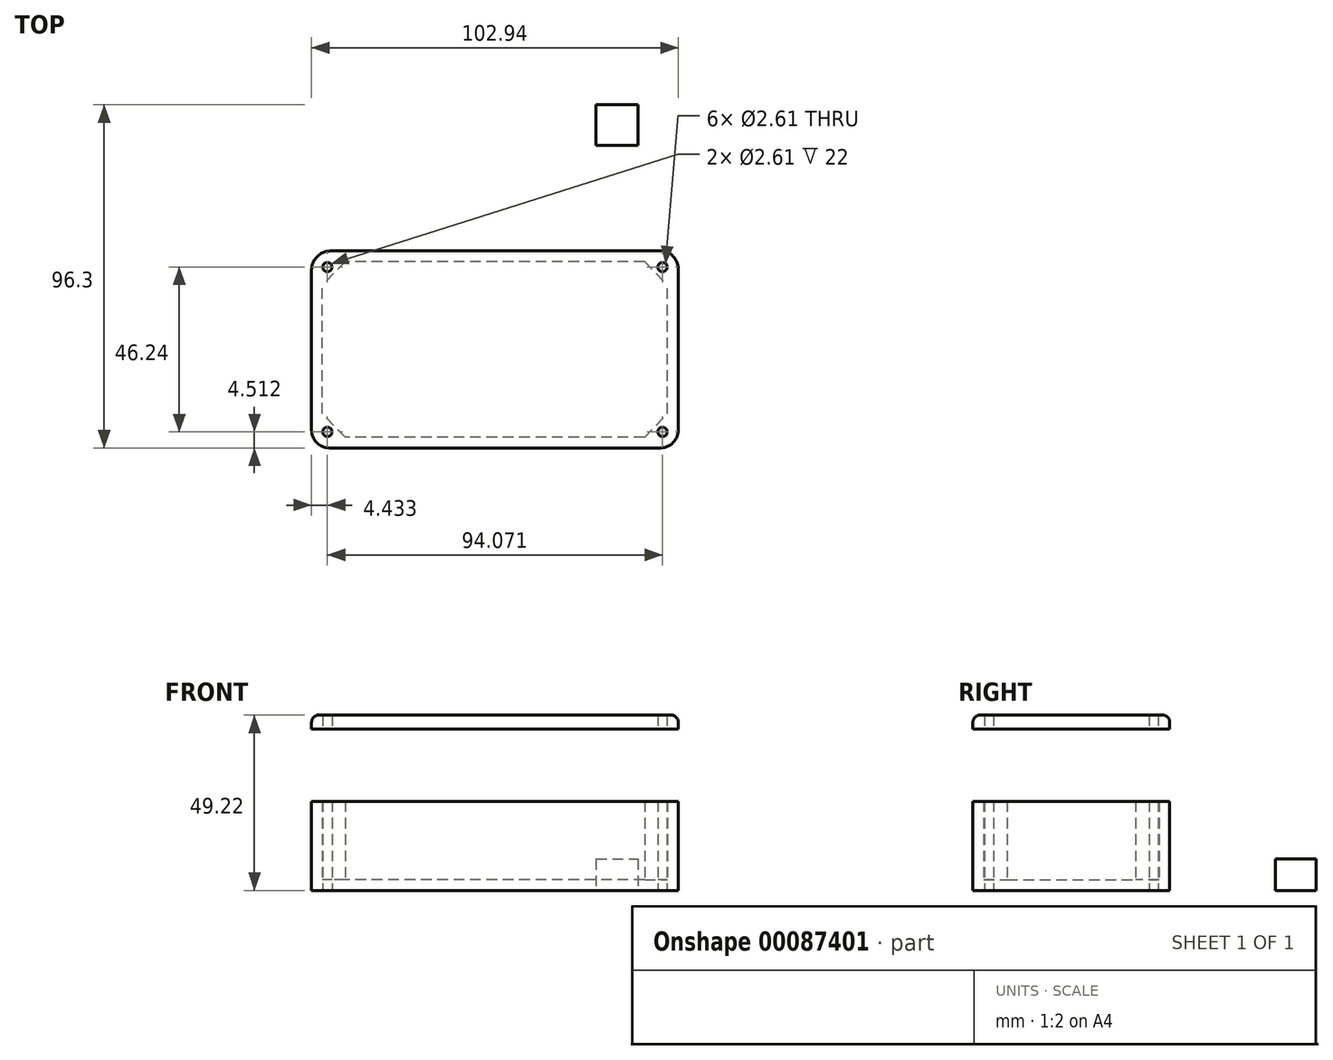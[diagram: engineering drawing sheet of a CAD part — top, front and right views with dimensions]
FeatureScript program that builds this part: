
annotation { "Feature Type Name" : "Feature", "Feature Type Description" : "" }
export const myFeature = defineFeature(function(context is Context, id is Id, definition is map)
    precondition{}
    {
        {
            var Q0;
            Q0=qCreatedBy(makeId("Top.planeOp"),FACE);
            var sketch = newSketch(context, id + "F0", { "sketchPlane" : qUnion([Q0])});
            skLineSegment(sketch, "E0.bottom", {"start": v(-57.78, 29.78) * mm, "end": v(34.86, 29.78) * mm});
            skLineSegment(sketch, "E0.top", {"start": v(-58.08, -25.48) * mm, "end": v(34.86, -25.48) * mm});
            skLineSegment(sketch, "E0.left", {"start": v(-63.08, 24.48) * mm, "end": v(-63.08, -20.48) * mm});
            skLineSegment(sketch, "E0.right", {"start": v(39.86, 24.78) * mm, "end": v(39.86, -20.48) * mm});
            skLineSegment(sketch, "E1.bottom", {"start": v(-11.61, 29.78) * mm, "end": v(-11.61, 29.78) * mm});
            skLineSegment(sketch, "E1.top", {"start": v(-11.61, -25.48) * mm, "end": v(-11.61, -25.48) * mm});
            skLineSegment(sketch, "E1.left", {"start": v(-11.61, 29.78) * mm, "end": v(-11.61, -25.48) * mm, "construction": true});
            skLineSegment(sketch, "E1.right", {"start": v(-11.61, 29.78) * mm, "end": v(-11.61, -25.48) * mm, "construction": true});
            skLineSegment(sketch, "E2", {"start": v(-63.08, 2.15) * mm, "end": v(39.86, 2.15) * mm, "construction": true});
            skPoint(sketch, "E3.visualSharp", {"position": v(-63.08, 29.78) * mm});
            skArc(sketch, "E3.filletArc", {"start": v(-57.78, 29.78) * mm, "mid": v(-61.53, 28.23) * mm, "end": v(-63.08, 24.48) * mm});
            skPoint(sketch, "E4.visualSharp", {"position": v(39.86, 29.78) * mm});
            skArc(sketch, "E4.filletArc", {"start": v(39.86, 24.78) * mm, "mid": v(38.4, 28.32) * mm, "end": v(34.86, 29.78) * mm});
            skPoint(sketch, "E5.visualSharp", {"position": v(39.86, -25.48) * mm});
            skArc(sketch, "E5.filletArc", {"start": v(34.86, -25.48) * mm, "mid": v(38.4, -24.01) * mm, "end": v(39.86, -20.48) * mm});
            skPoint(sketch, "E6.visualSharp", {"position": v(-63.08, -25.48) * mm});
            skArc(sketch, "E6.filletArc", {"start": v(-63.08, -20.48) * mm, "mid": v(-61.62, -24.01) * mm, "end": v(-58.08, -25.48) * mm});
            skArc(sketch, "E7.0", {"start": v(-57.78, 26.78) * mm, "mid": v(-59.4, 26.1) * mm, "end": v(-60.08, 24.48) * mm});
            skLineSegment(sketch, "E7.1", {"start": v(-57.78, 26.78) * mm, "end": v(34.86, 26.78) * mm});
            skLineSegment(sketch, "E7.2", {"start": v(-60.08, 24.48) * mm, "end": v(-60.08, -20.48) * mm});
            skArc(sketch, "E7.3", {"start": v(36.86, 24.78) * mm, "mid": v(36.27, 26.2) * mm, "end": v(34.86, 26.78) * mm});
            skArc(sketch, "E7.4", {"start": v(-60.08, -20.48) * mm, "mid": v(-59.5, -21.9) * mm, "end": v(-58.08, -22.48) * mm});
            skLineSegment(sketch, "E7.5", {"start": v(-58.08, -22.48) * mm, "end": v(34.86, -22.48) * mm});
            skArc(sketch, "E7.6", {"start": v(34.86, -22.48) * mm, "mid": v(36.27, -21.9) * mm, "end": v(36.86, -20.48) * mm});
            skLineSegment(sketch, "E7.7", {"start": v(36.86, 24.78) * mm, "end": v(36.86, -20.48) * mm});
            skCircle(sketch, "E8", {"center": v(-58.65, 25.27) * mm, "radius": 1.3 * mm});
            skLineSegment(sketch, "E9", {"start": v(-60.08, 20.2) * mm, "end": v(-53.64, 26.78) * mm});
            skCircle(sketch, "E10.MirrorC", {"center": v(35.42, 25.27) * mm, "radius": 1.3 * mm});
            skLineSegment(sketch, "E11.MirrorCS", {"start": v(36.86, 20.2) * mm, "end": v(30.41, 26.78) * mm});
            skCircle(sketch, "E12.MirrorC", {"center": v(35.42, -20.97) * mm, "radius": 1.3 * mm});
            skCircle(sketch, "E13.MirrorC", {"center": v(-58.65, -20.97) * mm, "radius": 1.3 * mm});
            skLineSegment(sketch, "E14.MirrorCS", {"start": v(-60.08, -15.9) * mm, "end": v(-53.64, -22.48) * mm});
            skLineSegment(sketch, "E15.MirrorCS", {"start": v(36.86, -15.9) * mm, "end": v(30.41, -22.48) * mm});
            skSolve(sketch);
        }
        {
            var Q0;
            Q0=qCreatedBy(makeId("Top.planeOp"),FACE);
            var sketch = newSketch(context, id + "F1", { "sketchPlane" : qUnion([Q0])});
            skLineSegment(sketch, "E16.bottom", {"start": v(16.8, 59.44) * mm, "end": v(28.5, 59.44) * mm});
            skLineSegment(sketch, "E16.top", {"start": v(16.8, 70.82) * mm, "end": v(28.5, 70.82) * mm});
            skLineSegment(sketch, "E16.left", {"start": v(16.8, 59.44) * mm, "end": v(16.8, 70.82) * mm});
            skLineSegment(sketch, "E16.right", {"start": v(28.5, 59.44) * mm, "end": v(28.5, 70.82) * mm});
            skSolve(sketch);
        }
        {
            var Q0;
            Q0=makeQuery(id+"F1.imprint","IMPRINT",FACE,{"disambiguationData":[TD([[makeQuery(id+"F1.imprint","IMPRINT",EDGE,{"derivedFrom":sQuery(id+"F1.wireOp",EDGE,"E16.bottom")}),1.0]])]});
            extrude(context, id + "F2", {"entities" : qUnion([Q0]), "depth" : 8.8 * mm});
        }
        {
            var Q0;
            {var subQ5=sQuery(id+"F0.wireOp",EDGE,"E9");Q0=makeQuery(id+"F0.imprint","IMPRINT",FACE,{"disambiguationData":[TD([[makeQuery(id+"F0.imprint","IMPRINT",EDGE,{"derivedFrom":subQ5}),-1.0]])]});}
            var Q1;
            Q1=makeQuery(id+"F0.imprint","IMPRINT",FACE,{"disambiguationData":[TD([[makeQuery(id+"F0.imprint","IMPRINT",EDGE,{"derivedFrom":sQuery(id+"F0.wireOp",EDGE,"E8")}),1.0]])]});
            var Q2;
            Q2=makeQuery(id+"F0.imprint","IMPRINT",FACE,{"disambiguationData":[TD([[makeQuery(id+"F0.imprint","IMPRINT",EDGE,{"derivedFrom":sQuery(id+"F0.wireOp",EDGE,"E13.MirrorC")}),-1.0]])]});
            var Q3;
            {var subQ1=sQuery(id+"F0.wireOp",EDGE,"E7.3");Q3=makeQuery(id+"F0.imprint","IMPRINT",FACE,{"disambiguationData":[TD([[makeQuery(id+"F0.imprint","IMPRINT",EDGE,{"derivedFrom":subQ1}),1.0]])]});}
            var Q4;
            {var subQ1=sQuery(id+"F0.wireOp",EDGE,"E7.4");Q4=makeQuery(id+"F0.imprint","IMPRINT",FACE,{"disambiguationData":[TD([[makeQuery(id+"F0.imprint","IMPRINT",EDGE,{"derivedFrom":subQ1}),1.0]])]});}
            var Q5;
            {var subQ1=sQuery(id+"F0.wireOp",EDGE,"E7.6");Q5=makeQuery(id+"F0.imprint","IMPRINT",FACE,{"disambiguationData":[TD([[makeQuery(id+"F0.imprint","IMPRINT",EDGE,{"derivedFrom":subQ1}),1.0]])]});}
            var Q6;
            Q6=makeQuery(id+"F0.imprint","IMPRINT",FACE,{"disambiguationData":[TD([[makeQuery(id+"F0.imprint","IMPRINT",EDGE,{"derivedFrom":sQuery(id+"F0.wireOp",EDGE,"E0.bottom")}),-1.0]])]});
            var Q7;
            Q7=makeQuery(id+"F0.imprint","IMPRINT",FACE,{"disambiguationData":[TD([[makeQuery(id+"F0.imprint","IMPRINT",EDGE,{"derivedFrom":sQuery(id+"F0.wireOp",EDGE,"E10.MirrorC")}),-1.0]])]});
            var Q8;
            {var subQ1=sQuery(id+"F0.wireOp",EDGE,"E7.0");Q8=makeQuery(id+"F0.imprint","IMPRINT",FACE,{"disambiguationData":[TD([[makeQuery(id+"F0.imprint","IMPRINT",EDGE,{"derivedFrom":subQ1}),1.0]])]});}
            var Q9;
            Q9=makeQuery(id+"F0.imprint","IMPRINT",FACE,{"disambiguationData":[TD([[makeQuery(id+"F0.imprint","IMPRINT",EDGE,{"derivedFrom":sQuery(id+"F0.wireOp",EDGE,"E12.MirrorC")}),1.0]])]});
            extrude(context, id + "F4", {"entities" : qUnion([Q0, Q1, Q2, Q3, Q4, Q5, Q6, Q7, Q8, Q9]), "depth" : 3 * mm});
        }
        {
            var Q0;
            Q0=makeQuery(id+"F0.imprint","IMPRINT",FACE,{"disambiguationData":[TD([[makeQuery(id+"F0.imprint","IMPRINT",EDGE,{"derivedFrom":sQuery(id+"F0.wireOp",EDGE,"E0.bottom")}),-1.0]])]});
            var Q1;
            {var subQ1=sQuery(id+"F0.wireOp",EDGE,"E7.6");Q1=makeQuery(id+"F0.imprint","IMPRINT",FACE,{"disambiguationData":[TD([[makeQuery(id+"F0.imprint","IMPRINT",EDGE,{"derivedFrom":subQ1}),1.0]])]});}
            var Q2;
            {var subQ1=sQuery(id+"F0.wireOp",EDGE,"E7.3");Q2=makeQuery(id+"F0.imprint","IMPRINT",FACE,{"disambiguationData":[TD([[makeQuery(id+"F0.imprint","IMPRINT",EDGE,{"derivedFrom":subQ1}),1.0]])]});}
            var Q3;
            {var subQ1=sQuery(id+"F0.wireOp",EDGE,"E7.0");Q3=makeQuery(id+"F0.imprint","IMPRINT",FACE,{"disambiguationData":[TD([[makeQuery(id+"F0.imprint","IMPRINT",EDGE,{"derivedFrom":subQ1}),1.0]])]});}
            var Q4;
            {var subQ1=sQuery(id+"F0.wireOp",EDGE,"E7.4");Q4=makeQuery(id+"F0.imprint","IMPRINT",FACE,{"disambiguationData":[TD([[makeQuery(id+"F0.imprint","IMPRINT",EDGE,{"derivedFrom":subQ1}),1.0]])]});}
            extrude(context, id + "F3", {"entities" : qUnion([Q0, Q1, Q2, Q3, Q4]), "operationType" : NewBodyOperationType.ADD, "depth" : 25 * mm});
        }
        {
            var Q0;
            {var subQ3=sQuery(id+"F0.wireOp",EDGE,"E15.MirrorCS");Q0=makeQuery(id+"F0.imprint","IMPRINT",FACE,{"disambiguationData":[TD([[makeQuery(id+"F0.imprint","IMPRINT",EDGE,{"derivedFrom":subQ3}),1.0]])]});}
            var Q1;
            {var subQ3=sQuery(id+"F0.wireOp",EDGE,"E9");Q1=makeQuery(id+"F0.imprint","IMPRINT",FACE,{"disambiguationData":[TD([[makeQuery(id+"F0.imprint","IMPRINT",EDGE,{"derivedFrom":subQ3}),1.0]])]});}
            var Q2;
            {var subQ8=sQuery(id+"F0.wireOp",EDGE,"E11.MirrorCS");Q2=makeQuery(id+"F0.imprint","IMPRINT",FACE,{"disambiguationData":[TD([[makeQuery(id+"F0.imprint","IMPRINT",EDGE,{"derivedFrom":subQ8}),-1.0]])]});}
            var Q3;
            {var subQ5=sQuery(id+"F0.wireOp",EDGE,"E9");Q3=makeQuery(id+"F0.imprint","IMPRINT",FACE,{"disambiguationData":[TD([[makeQuery(id+"F0.imprint","IMPRINT",EDGE,{"derivedFrom":subQ5}),-1.0]])]});}
            var Q4;
            {var subQ5=sQuery(id+"F0.wireOp",EDGE,"E14.MirrorCS");Q4=makeQuery(id+"F0.imprint","IMPRINT",FACE,{"disambiguationData":[TD([[makeQuery(id+"F0.imprint","IMPRINT",EDGE,{"derivedFrom":subQ5}),-1.0]])]});}
            var Q5;
            Q5=makeQuery(id+"F0.imprint","IMPRINT",FACE,{"disambiguationData":[TD([[makeQuery(id+"F0.imprint","IMPRINT",EDGE,{"derivedFrom":sQuery(id+"F0.wireOp",EDGE,"E0.bottom")}),-1.0]])]});
            extrude(context, id + "F5", {"entities" : qUnion([Q0, Q1, Q2, Q3, Q4, Q5]), "depth" : 49.22 * mm, "hasSecondDirection" : true, "secondDirectionOppositeDirection" : false, "secondDirectionDepth" : 45.3 * mm});
        }
        {
            var Q0;
            Q0=makeQuery(id+"F5.opExtrude","CAP_EDGE",EDGE,{"disambiguationData":[OSD([sQuery(id+"F0.wireOp",EDGE,"E0.bottom")])],"isStart":false});
            var Q1;
            Q1=makeQuery(id+"F5.opExtrude","CAP_EDGE",EDGE,{"disambiguationData":[OSD([sQuery(id+"F0.wireOp",EDGE,"E0.left")])],"isStart":false});
            fillet(context, id + "F6", {"entities" : qUnion([Q0, Q1]), "radius" : 2 * mm, "tangentPropagation" : true, "allowEdgeOverflow" : false});
        }
    });
